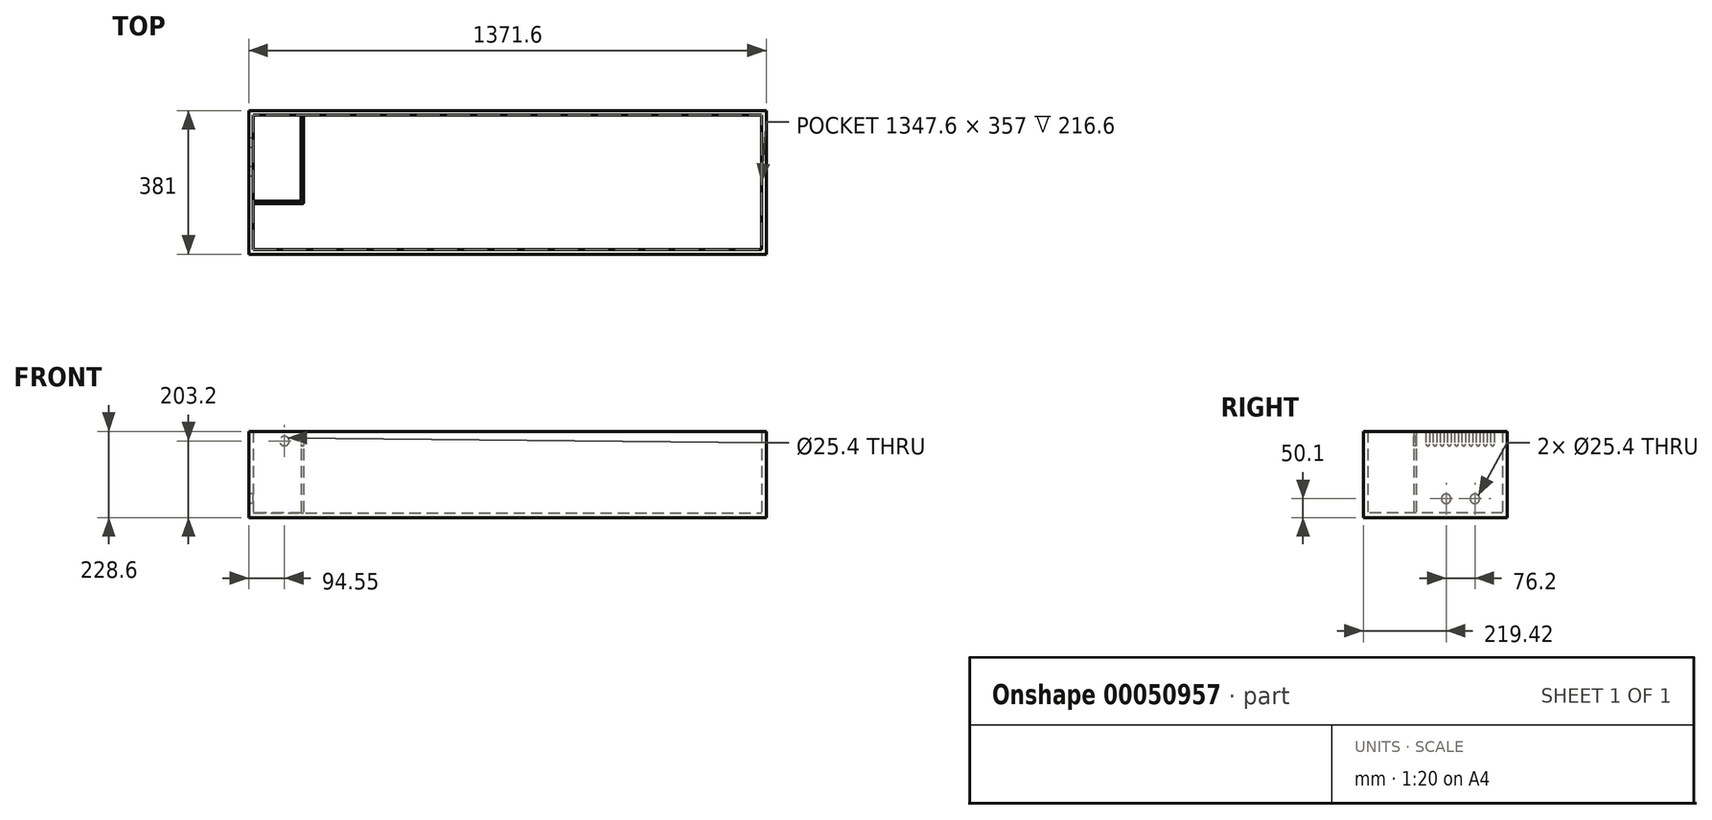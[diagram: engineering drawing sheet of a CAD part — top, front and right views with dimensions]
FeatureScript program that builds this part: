
annotation { "Feature Type Name" : "Feature", "Feature Type Description" : "" }
export const myFeature = defineFeature(function(context is Context, id is Id, definition is map)
    precondition{}
    {
        {
            var Q0;
            Q0=qCreatedBy(makeId("Top.planeOp"),FACE);
            var sketch = newSketch(context, id + "F0", { "sketchPlane" : qUnion([Q0])});
            skLineSegment(sketch, "E0.bottom", {"start": v(-696.4, 161.58) * mm, "end": v(675.2, 161.58) * mm});
            skLineSegment(sketch, "E0.top", {"start": v(-696.4, -219.42) * mm, "end": v(675.2, -219.42) * mm});
            skLineSegment(sketch, "E0.left", {"start": v(-696.4, 161.58) * mm, "end": v(-696.4, -219.42) * mm});
            skLineSegment(sketch, "E0.right", {"start": v(675.2, 161.58) * mm, "end": v(675.2, -219.42) * mm});
            skSolve(sketch);
        }
        {
            var Q0;
            Q0=makeQuery(id+"F0.imprint","IMPRINT",FACE,{"disambiguationData":[TD([[makeQuery(id+"F0.imprint","IMPRINT",EDGE,{"derivedFrom":sQuery(id+"F0.wireOp",EDGE,"E0.bottom")}),-1.0]])]});
            extrude(context, id + "F1", {"entities" : qUnion([Q0]), "depth" : 228.6 * mm});
        }
        {
            var Q0;
            Q0=makeQuery(id+"F1.opExtrude","CAP_FACE",FACE,{"disambiguationData":[OSD([sQuery(id+"F0.wireOp",EDGE,"E0.bottom"),sQuery(id+"F0.wireOp",EDGE,"E0.top"),sQuery(id+"F0.wireOp",EDGE,"E0.left"),sQuery(id+"F0.wireOp",EDGE,"E0.right")])],"isStart":false});
            shell(context, id + "F2", {"entities" : qUnion([Q0]), "thickness" : 12 * mm});
        }
        {
            var Q0;
            Q0=makeQuery(id+"F2.opShell","OFFSET_FACE",FACE,{"disambiguationData":[OSD([sQuery(id+"F0.wireOp",EDGE,"E0.bottom"),sQuery(id+"F0.wireOp",EDGE,"E0.top"),sQuery(id+"F0.wireOp",EDGE,"E0.left"),sQuery(id+"F0.wireOp",EDGE,"E0.right")])]});
            var sketch = newSketch(context, id + "F3", { "sketchPlane" : qUnion([Q0])});
            skLineSegment(sketch, "E1.bottom", {"start": v(-557.4, 149.58) * mm, "end": v(-551.05, 149.58) * mm});
            skLineSegment(sketch, "E1.top", {"start": v(-684.4, -85.37) * mm, "end": v(-551.05, -85.37) * mm});
            skLineSegment(sketch, "E1.left", {"start": v(-684.4, -79.02) * mm, "end": v(-684.4, -85.37) * mm});
            skLineSegment(sketch, "E1.right", {"start": v(-551.05, 149.58) * mm, "end": v(-551.05, -85.37) * mm});
            skLineSegment(sketch, "E2", {"start": v(-557.4, 149.58) * mm, "end": v(-557.4, -79.02) * mm});
            skLineSegment(sketch, "E3", {"start": v(-557.4, -79.02) * mm, "end": v(-684.4, -79.02) * mm});
            skSolve(sketch);
        }
        {
            var Q0;
            Q0 = qSketchRegion(id + "F3", true);
            extrude(context, id + "F4", {"entities" : qUnion([Q0]), "depth" : 216.6 * mm});
        }
        {
            var Q0;
            Q0=makeQuery(id+"F4.opExtrude","SWEPT_FACE",FACE,{"disambiguationData":[OSD([sQuery(id+"F3.wireOp",EDGE,"E1.top")])]});
            var sketch = newSketch(context, id + "F5", { "sketchPlane" : qUnion([Q0])});
            skCircle(sketch, "E4", {"center": v(-601.85, 203.2) * mm, "radius": 12.7 * mm});
            skSolve(sketch);
        }
        {
            var Q0;
            Q0 = qSketchRegion(id + "F5", true);
            extrude(context, id + "F6", {"entities" : qUnion([Q0]), "operationType" : NewBodyOperationType.REMOVE, "oppositeDirection" : true, "depth" : 25.4 * mm});
        }
        {
            var Q0;
            Q0=makeQuery(id+"F4.opExtrude","SWEPT_FACE",FACE,{"disambiguationData":[OSD([sQuery(id+"F3.wireOp",EDGE,"E1.right")])]});
            var sketch = newSketch(context, id + "F7", { "sketchPlane" : qUnion([Q0])});
            skLineSegment(sketch, "E5.bottom", {"start": v(-53.62, 228.6) * mm, "end": v(-43.62, 228.6) * mm});
            skLineSegment(sketch, "E5.left", {"start": v(-53.62, 228.6) * mm, "end": v(-53.62, 195.5) * mm});
            skLineSegment(sketch, "E5.right", {"start": v(-43.62, 228.6) * mm, "end": v(-43.62, 195.5) * mm});
            skPoint(sketch, "E6.visualSharp", {"position": v(-53.62, 211.1) * mm});
            skArc(sketch, "E6.filletArc", {"start": v(-53.62, 195.5) * mm, "mid": v(-48.62, 190.5) * mm, "end": v(-43.62, 195.5) * mm});
            skLineSegment(sketch, "E7.1.0.0", {"start": v(-34.57, 228.6) * mm, "end": v(-34.57, 195.5) * mm});
            skArc(sketch, "E7.1.0.1", {"start": v(-34.57, 195.5) * mm, "mid": v(-29.57, 190.5) * mm, "end": v(-24.57, 195.5) * mm});
            skLineSegment(sketch, "E7.1.0.2", {"start": v(-24.57, 228.6) * mm, "end": v(-24.57, 195.5) * mm});
            skLineSegment(sketch, "E7.1.0.3", {"start": v(-34.57, 228.6) * mm, "end": v(-24.57, 228.6) * mm});
            skLineSegment(sketch, "E7.2.0.0", {"start": v(-15.52, 228.6) * mm, "end": v(-15.52, 195.5) * mm});
            skArc(sketch, "E7.2.0.1", {"start": v(-15.52, 195.5) * mm, "mid": v(-10.52, 190.5) * mm, "end": v(-5.52, 195.5) * mm});
            skLineSegment(sketch, "E7.2.0.2", {"start": v(-5.52, 228.6) * mm, "end": v(-5.52, 195.5) * mm});
            skLineSegment(sketch, "E7.2.0.3", {"start": v(-15.52, 228.6) * mm, "end": v(-5.52, 228.6) * mm});
            skLineSegment(sketch, "E7.3.0.0", {"start": v(3.53, 228.6) * mm, "end": v(3.53, 195.5) * mm});
            skArc(sketch, "E7.3.0.1", {"start": v(3.53, 195.5) * mm, "mid": v(8.53, 190.5) * mm, "end": v(13.53, 195.5) * mm});
            skLineSegment(sketch, "E7.3.0.2", {"start": v(13.53, 228.6) * mm, "end": v(13.53, 195.5) * mm});
            skLineSegment(sketch, "E7.3.0.3", {"start": v(3.53, 228.6) * mm, "end": v(13.53, 228.6) * mm});
            skLineSegment(sketch, "E7.4.0.0", {"start": v(22.58, 228.6) * mm, "end": v(22.58, 195.5) * mm});
            skArc(sketch, "E7.4.0.1", {"start": v(22.58, 195.5) * mm, "mid": v(27.58, 190.5) * mm, "end": v(32.58, 195.5) * mm});
            skLineSegment(sketch, "E7.4.0.2", {"start": v(32.58, 228.6) * mm, "end": v(32.58, 195.5) * mm});
            skLineSegment(sketch, "E7.4.0.3", {"start": v(22.58, 228.6) * mm, "end": v(32.58, 228.6) * mm});
            skLineSegment(sketch, "E7.5.0.0", {"start": v(41.63, 228.6) * mm, "end": v(41.63, 195.5) * mm});
            skArc(sketch, "E7.5.0.1", {"start": v(41.63, 195.5) * mm, "mid": v(46.63, 190.5) * mm, "end": v(51.63, 195.5) * mm});
            skLineSegment(sketch, "E7.5.0.2", {"start": v(51.63, 228.6) * mm, "end": v(51.63, 195.5) * mm});
            skLineSegment(sketch, "E7.5.0.3", {"start": v(41.63, 228.6) * mm, "end": v(51.63, 228.6) * mm});
            skLineSegment(sketch, "E7.6.0.0", {"start": v(60.68, 228.6) * mm, "end": v(60.68, 195.5) * mm});
            skArc(sketch, "E7.6.0.1", {"start": v(60.68, 195.5) * mm, "mid": v(65.68, 190.5) * mm, "end": v(70.68, 195.5) * mm});
            skLineSegment(sketch, "E7.6.0.2", {"start": v(70.68, 228.6) * mm, "end": v(70.68, 195.5) * mm});
            skLineSegment(sketch, "E7.6.0.3", {"start": v(60.68, 228.6) * mm, "end": v(70.68, 228.6) * mm});
            skLineSegment(sketch, "E7.7.0.0", {"start": v(79.73, 228.6) * mm, "end": v(79.73, 195.5) * mm});
            skArc(sketch, "E7.7.0.1", {"start": v(79.73, 195.5) * mm, "mid": v(84.73, 190.5) * mm, "end": v(89.73, 195.5) * mm});
            skLineSegment(sketch, "E7.7.0.2", {"start": v(89.73, 228.6) * mm, "end": v(89.73, 195.5) * mm});
            skLineSegment(sketch, "E7.7.0.3", {"start": v(79.73, 228.6) * mm, "end": v(89.73, 228.6) * mm});
            skLineSegment(sketch, "E7.8.0.0", {"start": v(98.78, 228.6) * mm, "end": v(98.78, 195.5) * mm});
            skArc(sketch, "E7.8.0.1", {"start": v(98.78, 195.5) * mm, "mid": v(103.78, 190.5) * mm, "end": v(108.78, 195.5) * mm});
            skLineSegment(sketch, "E7.8.0.2", {"start": v(108.78, 228.6) * mm, "end": v(108.78, 195.5) * mm});
            skLineSegment(sketch, "E7.8.0.3", {"start": v(98.78, 228.6) * mm, "end": v(108.78, 228.6) * mm});
            skLineSegment(sketch, "E7.9.0.0", {"start": v(117.83, 228.6) * mm, "end": v(117.83, 195.5) * mm});
            skArc(sketch, "E7.9.0.1", {"start": v(117.83, 195.5) * mm, "mid": v(122.83, 190.5) * mm, "end": v(127.83, 195.5) * mm});
            skLineSegment(sketch, "E7.9.0.2", {"start": v(127.83, 228.6) * mm, "end": v(127.83, 195.5) * mm});
            skLineSegment(sketch, "E7.9.0.3", {"start": v(117.83, 228.6) * mm, "end": v(127.83, 228.6) * mm});
            skLineSegment(sketch, "E7.direction1", {"start": v(-72.67, 195.5) * mm, "end": v(-53.62, 195.5) * mm, "construction": true});
            skSolve(sketch);
        }
        {
            var Q0;
            Q0 = qSketchRegion(id + "F7", true);
            extrude(context, id + "F8", {"entities" : qUnion([Q0]), "operationType" : NewBodyOperationType.REMOVE, "oppositeDirection" : true, "depth" : 25.4 * mm});
        }
        {
            var Q0;
            Q0=makeQuery(id+"F1.opExtrude","SWEPT_FACE",FACE,{"disambiguationData":[OSD([sQuery(id+"F0.wireOp",EDGE,"E0.left")])]});
            var sketch = newSketch(context, id + "F9", { "sketchPlane" : qUnion([Q0])});
            skCircle(sketch, "E8", {"center": v(-76.2, 50.1) * mm, "radius": 12.7 * mm});
            skCircle(sketch, "E9", {"center": v(0, 50.1) * mm, "radius": 12.7 * mm});
            skSolve(sketch);
        }
        {
            var Q0;
            Q0 = qSketchRegion(id + "F9", true);
            extrude(context, id + "F10", {"entities" : qUnion([Q0]), "operationType" : NewBodyOperationType.REMOVE, "oppositeDirection" : true, "depth" : 25.4 * mm});
        }
    });
